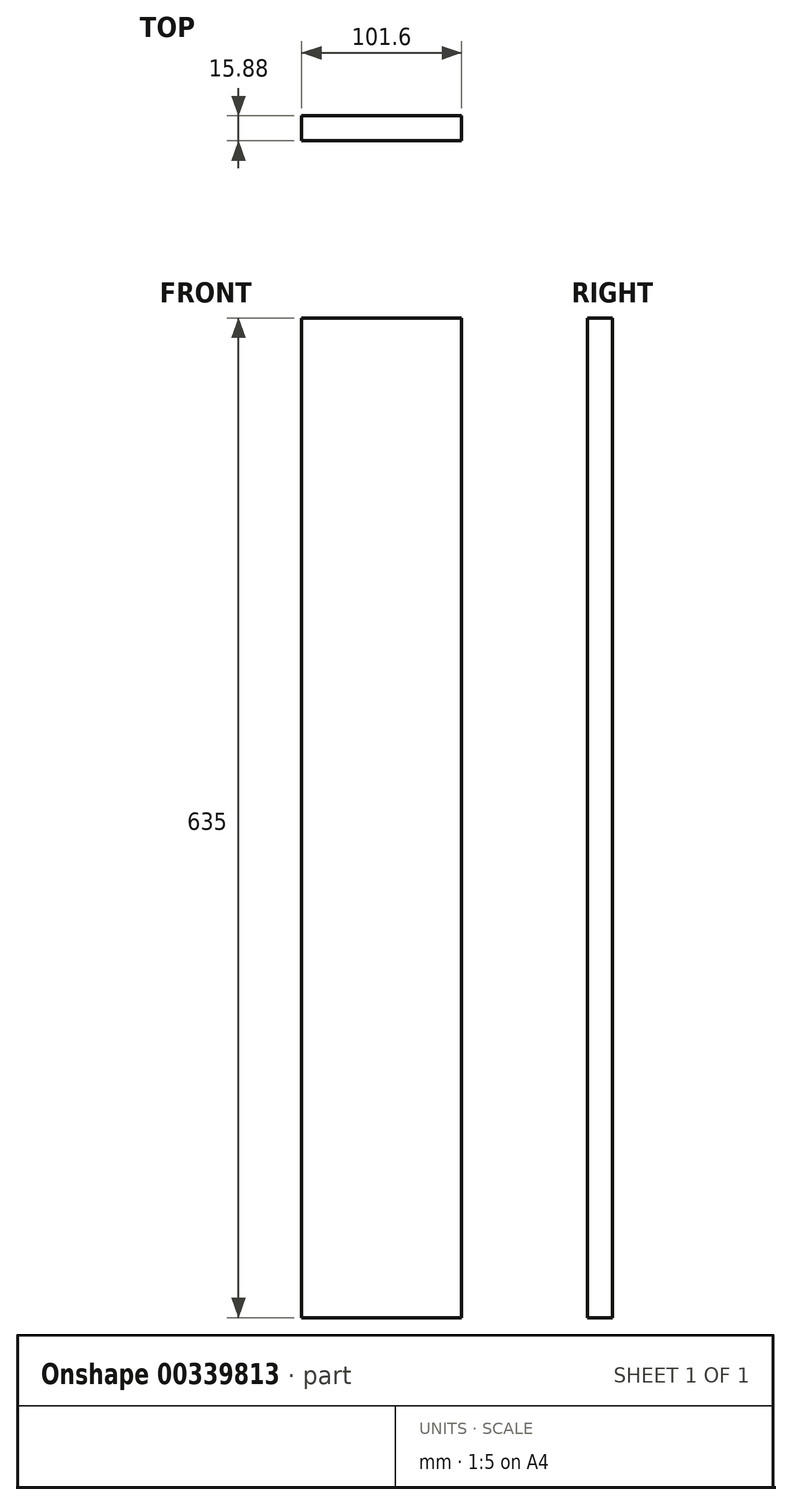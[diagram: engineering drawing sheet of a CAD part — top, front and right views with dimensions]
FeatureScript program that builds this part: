
annotation { "Feature Type Name" : "Feature", "Feature Type Description" : "" }
export const myFeature = defineFeature(function(context is Context, id is Id, definition is map)
    precondition{}
    {
        {
            var Q0;
            Q0=qCreatedBy(makeId("Front.planeOp"),FACE);
            var sketch = newSketch(context, id + "F0", { "sketchPlane" : qUnion([Q0])});
            skLineSegment(sketch, "E0.bottom", {"start": v(-56.36, 510.44) * mm, "end": v(45.24, 510.44) * mm});
            skLineSegment(sketch, "E0.top", {"start": v(-56.36, -124.56) * mm, "end": v(45.24, -124.56) * mm});
            skLineSegment(sketch, "E0.left", {"start": v(-56.36, 510.44) * mm, "end": v(-56.36, -124.56) * mm});
            skLineSegment(sketch, "E0.right", {"start": v(45.24, 510.44) * mm, "end": v(45.24, -124.56) * mm});
            skSolve(sketch);
        }
        {
            var Q0;
            Q0 = qSketchRegion(id + "F0", true);
            extrude(context, id + "F1", {"entities" : qUnion([Q0]), "oppositeDirection" : true, "depth" : 15.88 * mm});
        }
    });
